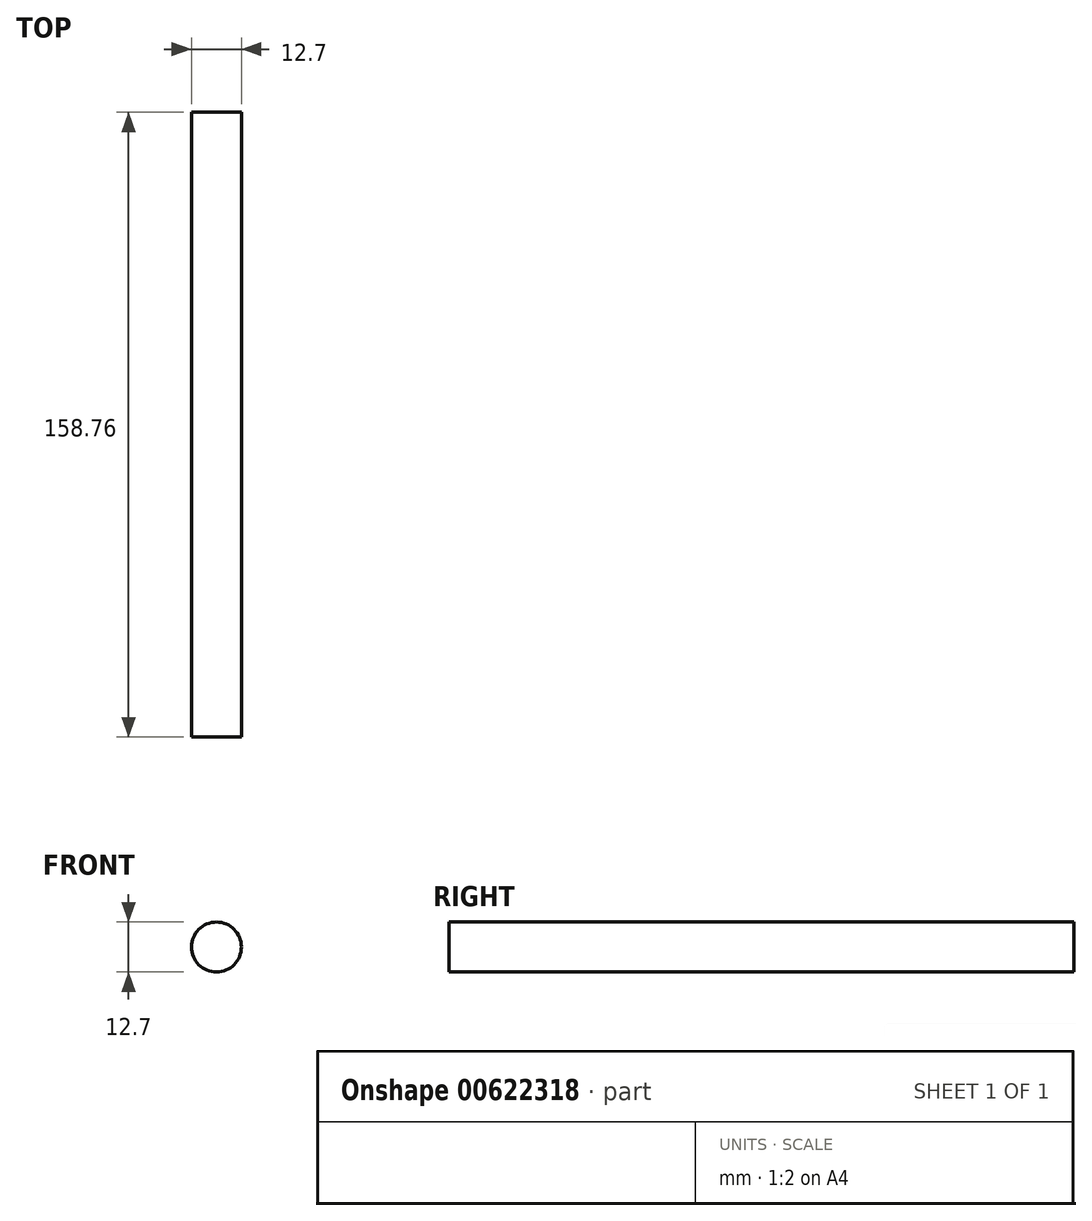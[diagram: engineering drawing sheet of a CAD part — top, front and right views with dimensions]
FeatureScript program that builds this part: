
annotation { "Feature Type Name" : "Feature", "Feature Type Description" : "" }
export const myFeature = defineFeature(function(context is Context, id is Id, definition is map)
    precondition{}
    {
        {
            var Q0;
            Q0=qCreatedBy(makeId("Front.planeOp"),FACE);
            var sketch = newSketch(context, id + "F0", { "sketchPlane" : qUnion([Q0])});
            skCircle(sketch, "E0", {"center": v(0, 0) * mm, "radius": 6.35 * mm});
            skSolve(sketch);
        }
        {
            var Q0;
            Q0=makeQuery(id+"F0.imprint","IMPRINT",FACE,{"disambiguationData":[TD([[makeQuery(id+"F0.imprint","IMPRINT",EDGE,{"derivedFrom":sQuery(id+"F0.wireOp",EDGE,"E0")}),1.0]])]});
            extrude(context, id + "F1", {"entities" : qUnion([Q0]), "depth" : 158.75 * mm, "offsetDistance" : 25.4 * mm, "symmetric" : true});
        }
    });
